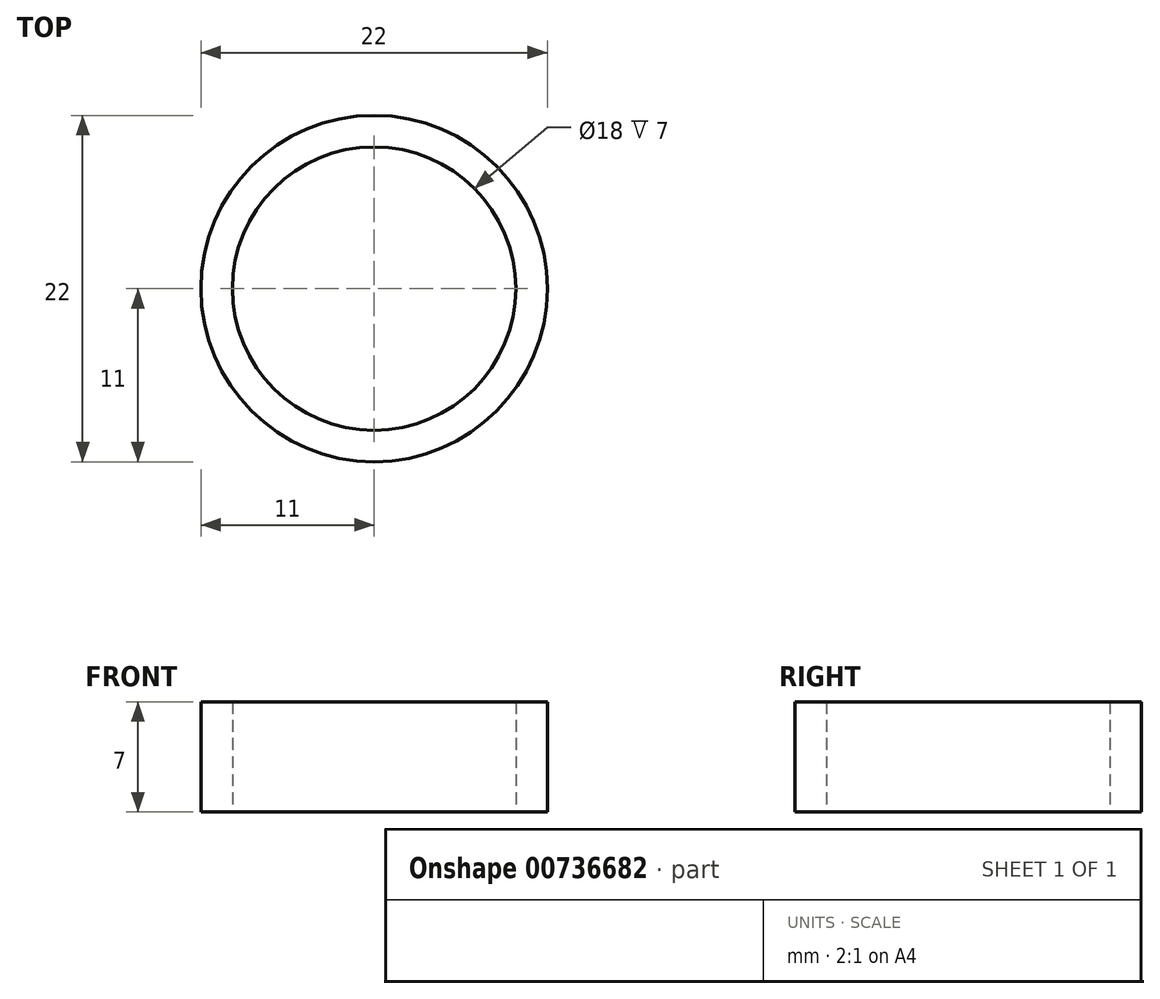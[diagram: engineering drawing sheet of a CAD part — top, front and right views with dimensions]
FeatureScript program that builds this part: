
annotation { "Feature Type Name" : "Feature", "Feature Type Description" : "" }
export const myFeature = defineFeature(function(context is Context, id is Id, definition is map)
    precondition{}
    {
        {
            var Q0;
            Q0=qCreatedBy(makeId("Top.planeOp"),FACE);
            var sketch = newSketch(context, id + "F0", { "sketchPlane" : qUnion([Q0])});
            skCircle(sketch, "E0", {"center": v(0, 0) * mm, "radius": 11 * mm});
            skCircle(sketch, "E1", {"center": v(0, 0) * mm, "radius": 9 * mm});
            skSolve(sketch);
        }
        {
            var Q0;
            Q0=makeQuery(id+"F0.imprint","IMPRINT",FACE,{"disambiguationData":[TD([[makeQuery(id+"F0.imprint","IMPRINT",EDGE,{"derivedFrom":sQuery(id+"F0.wireOp",EDGE,"E0")}),1.0]])]});
            extrude(context, id + "F1", {"entities" : qUnion([Q0]), "depth" : 7 * mm, "offsetDistance" : 25 * mm});
        }
    });
